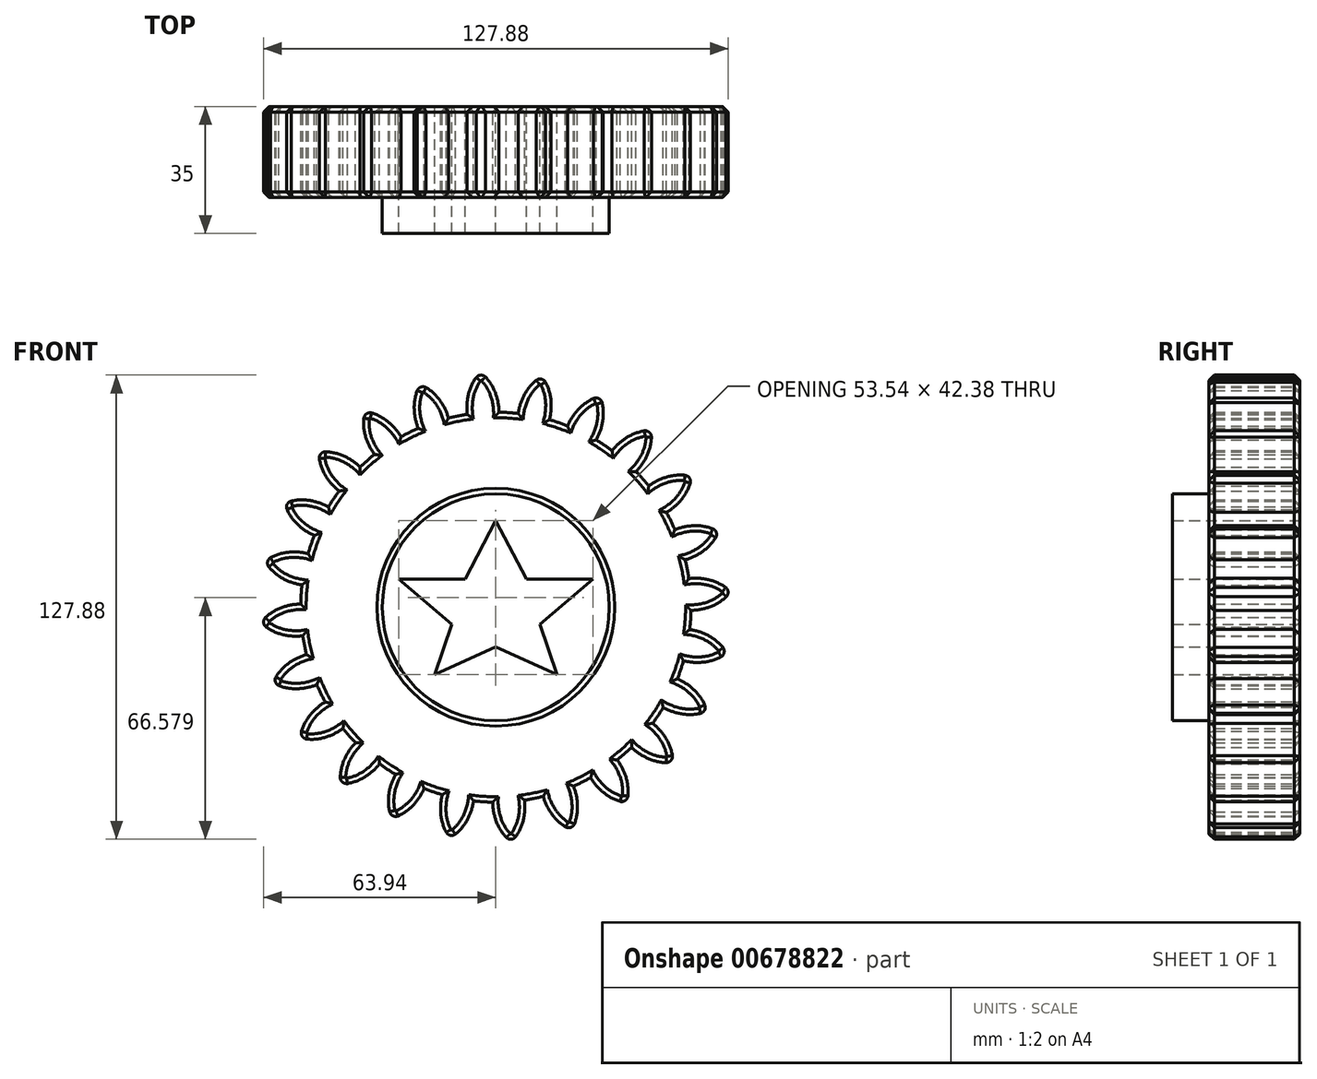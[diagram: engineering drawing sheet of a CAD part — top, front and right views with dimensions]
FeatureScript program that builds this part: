
annotation { "Feature Type Name" : "Feature", "Feature Type Description" : "" }
export const myFeature = defineFeature(function(context is Context, id is Id, definition is map)
    precondition{}
    {
        {
            var Q0;
            Q0=qCreatedBy(makeId("Front.planeOp"),FACE);
            var sketch = newSketch(context, id + "F0", { "sketchPlane" : qUnion([Q0])});
            skCircle(sketch, "E0", {"center": v(0, 0) * mm, "radius": 53.72 * mm});
            skCircle(sketch, "E1", {"center": v(0, 0) * mm, "radius": 58.67 * mm, "construction": true});
            skCircle(sketch, "E2", {"center": v(0, 0) * mm, "radius": 63.5 * mm, "construction": true});
            skLineSegment(sketch, "E3", {"start": v(0, 0) * mm, "end": v(0, 90.28) * mm, "construction": true});
            skLineSegment(sketch, "E4", {"start": v(0, 0) * mm, "end": v(-5.89, 89.83) * mm, "construction": true});
            skLineSegment(sketch, "E5", {"start": v(0, 58.67) * mm, "end": v(-86.47, 27.2) * mm, "construction": true});
            skLineSegment(sketch, "E6", {"start": v(0, 58.67) * mm, "end": v(-89.07, 58.67) * mm, "construction": true});
            skCircle(sketch, "E7", {"center": v(0, 0) * mm, "radius": 55.14 * mm, "construction": true});
            skCircle(sketch, "E8", {"center": v(0, 58.67) * mm, "radius": 14.6 * mm, "construction": true});
            skCircle(sketch, "E9", {"center": v(-13.72, 53.68) * mm, "radius": 14.6 * mm, "construction": true});
            skArc(sketch, "E10", {"start": v(0, 58.67) * mm, "mid": v(-1.18, 61.2) * mm, "end": v(-2.86, 63.44) * mm});
            skArc(sketch, "E11", {"start": v(0.88, 53.71) * mm, "mid": v(0.64, 56.23) * mm, "end": v(0, 58.67) * mm});
            skArc(sketch, "E12.MirrorCS", {"start": v(-7.88, 53.14) * mm, "mid": v(-7.97, 55.66) * mm, "end": v(-7.66, 58.17) * mm});
            skArc(sketch, "E13.MirrorCS", {"start": v(-7.66, 58.17) * mm, "mid": v(-6.82, 60.83) * mm, "end": v(-5.45, 63.27) * mm});
            skArc(sketch, "E14", {"start": v(-2.86, 63.44) * mm, "mid": v(-4.2, 63.93) * mm, "end": v(-5.45, 63.27) * mm});
            skCircle(sketch, "E15", {"center": v(0, 0) * mm, "radius": 31.25 * mm});
            skLineSegment(sketch, "E16", {"start": v(0, 23.83) * mm, "end": v(8.38, 7.72) * mm});
            skLineSegment(sketch, "E17", {"start": v(8.38, 7.72) * mm, "end": v(26.77, 7.72) * mm});
            skLineSegment(sketch, "E18", {"start": v(26.77, 7.72) * mm, "end": v(12.19, -4.72) * mm});
            skLineSegment(sketch, "E19", {"start": v(12.19, -4.72) * mm, "end": v(16.83, -18.55) * mm});
            skLineSegment(sketch, "E20", {"start": v(16.83, -18.55) * mm, "end": v(0, -10.88) * mm});
            skLineSegment(sketch, "E21.MirrorCS", {"start": v(0, 23.83) * mm, "end": v(-8.38, 7.72) * mm});
            skLineSegment(sketch, "E22.MirrorCS", {"start": v(-8.38, 7.72) * mm, "end": v(-26.77, 7.72) * mm});
            skLineSegment(sketch, "E23.MirrorCS", {"start": v(-26.77, 7.72) * mm, "end": v(-12.19, -4.72) * mm});
            skLineSegment(sketch, "E24.MirrorCS", {"start": v(-12.19, -4.72) * mm, "end": v(-16.83, -18.55) * mm});
            skLineSegment(sketch, "E25.MirrorCS", {"start": v(-16.83, -18.55) * mm, "end": v(0, -10.88) * mm});
            skSolve(sketch);
        }
        {
            var Q0;
            {var subQ0=sQuery(id+"F0.wireOp",EDGE,"E0");var subQ1=makeQuery(id+"F0.imprint","INTERSECT",VERTEX,{"derivedFrom":[subQ0,sQuery(id+"F0.wireOp",EDGE,"E12.MirrorCS")]});Q0=makeQuery(id+"F0.imprint","IMPRINT",FACE,{"disambiguationData":[TD([[makeQuery(id+"F0.imprint","IMPRINT",EDGE,{"disambiguationData":[TD([[subQ1,1.0]])],"derivedFrom":subQ0}),1.0]])]});}
            var Q1;
            Q1=makeQuery(id+"F0.imprint","IMPRINT",FACE,{"disambiguationData":[TD([[makeQuery(id+"F0.imprint","IMPRINT",EDGE,{"derivedFrom":sQuery(id+"F0.wireOp",EDGE,"E10")}),1.0]])]});
            extrude(context, id + "F1", {"entities" : qUnion([Q0, Q1]), "depth" : 25 * mm, "offsetDistance" : 25 * mm});
        }
        {
            var Q0;
            Q0=makeQuery(id+"F1.opExtrude","SWEPT_BODY",BODY,{"disambiguationData":[OSD([sQuery(id+"F0.wireOp",EDGE,"E0"),sQuery(id+"F0.wireOp",EDGE,"E10"),sQuery(id+"F0.wireOp",EDGE,"E12.MirrorCS"),sQuery(id+"F0.wireOp",EDGE,"E13.MirrorCS"),sQuery(id+"F0.wireOp",EDGE,"E11"),sQuery(id+"F0.wireOp",EDGE,"E14")])]});
            var Q1;
            Q1=makeQuery(id+"F1.opExtrude","SWEPT_FACE",FACE,{"disambiguationData":[OSD([sQuery(id+"F0.wireOp",EDGE,"E0")])]});
            circularPattern(context, id + "F2", {"entities" : qUnion([Q0]), "axis" : qUnion([Q1]), "angle" : 360 * degree, "instanceCount" : 24, "equalSpace" : true});
        }
        {
            var Q0;
            {var subQ0=makeQuery(id+"F1.opExtrude","CAP_FACE",FACE,{"disambiguationData":[OSD([sQuery(id+"F0.wireOp",EDGE,"E0"),sQuery(id+"F0.wireOp",EDGE,"E10"),sQuery(id+"F0.wireOp",EDGE,"E12.MirrorCS"),sQuery(id+"F0.wireOp",EDGE,"E13.MirrorCS"),sQuery(id+"F0.wireOp",EDGE,"E11"),sQuery(id+"F0.wireOp",EDGE,"E14"),sQuery(id+"F0.wireOp",EDGE,"E16"),sQuery(id+"F0.wireOp",EDGE,"E17"),sQuery(id+"F0.wireOp",EDGE,"E18"),sQuery(id+"F0.wireOp",EDGE,"E19"),sQuery(id+"F0.wireOp",EDGE,"E20"),sQuery(id+"F0.wireOp",EDGE,"E21.MirrorCS"),sQuery(id+"F0.wireOp",EDGE,"E22.MirrorCS"),sQuery(id+"F0.wireOp",EDGE,"E23.MirrorCS"),sQuery(id+"F0.wireOp",EDGE,"E24.MirrorCS"),sQuery(id+"F0.wireOp",EDGE,"E25.MirrorCS")])],"isStart":false});Q0=makeQuery(id+"FgwtWg0tSMJMYA0_0.boolean.opBoolean","MERGE",FACE,{"derivedFrom":[subQ0,makeQuery(id+"F2.opPattern","COPY",FACE,{"derivedFrom":subQ0,"instanceName":"1"}),makeQuery(id+"F2.opPattern","COPY",FACE,{"derivedFrom":subQ0,"instanceName":"2"}),makeQuery(id+"F2.opPattern","COPY",FACE,{"derivedFrom":subQ0,"instanceName":"3"}),makeQuery(id+"F2.opPattern","COPY",FACE,{"derivedFrom":subQ0,"instanceName":"4"}),makeQuery(id+"F2.opPattern","COPY",FACE,{"derivedFrom":subQ0,"instanceName":"5"}),makeQuery(id+"F2.opPattern","COPY",FACE,{"derivedFrom":subQ0,"instanceName":"6"}),makeQuery(id+"F2.opPattern","COPY",FACE,{"derivedFrom":subQ0,"instanceName":"7"}),makeQuery(id+"F2.opPattern","COPY",FACE,{"derivedFrom":subQ0,"instanceName":"8"}),makeQuery(id+"F2.opPattern","COPY",FACE,{"derivedFrom":subQ0,"instanceName":"9"}),makeQuery(id+"F2.opPattern","COPY",FACE,{"derivedFrom":subQ0,"instanceName":"10"}),makeQuery(id+"F2.opPattern","COPY",FACE,{"derivedFrom":subQ0,"instanceName":"11"}),makeQuery(id+"F2.opPattern","COPY",FACE,{"derivedFrom":subQ0,"instanceName":"12"}),makeQuery(id+"F2.opPattern","COPY",FACE,{"derivedFrom":subQ0,"instanceName":"13"}),makeQuery(id+"F2.opPattern","COPY",FACE,{"derivedFrom":subQ0,"instanceName":"14"}),makeQuery(id+"F2.opPattern","COPY",FACE,{"derivedFrom":subQ0,"instanceName":"15"}),makeQuery(id+"F2.opPattern","COPY",FACE,{"derivedFrom":subQ0,"instanceName":"16"}),makeQuery(id+"F2.opPattern","COPY",FACE,{"derivedFrom":subQ0,"instanceName":"17"}),makeQuery(id+"F2.opPattern","COPY",FACE,{"derivedFrom":subQ0,"instanceName":"18"}),makeQuery(id+"F2.opPattern","COPY",FACE,{"derivedFrom":subQ0,"instanceName":"19"}),makeQuery(id+"F2.opPattern","COPY",FACE,{"derivedFrom":subQ0,"instanceName":"20"}),makeQuery(id+"F2.opPattern","COPY",FACE,{"derivedFrom":subQ0,"instanceName":"21"}),makeQuery(id+"F2.opPattern","COPY",FACE,{"derivedFrom":subQ0,"instanceName":"22"}),makeQuery(id+"F2.opPattern","COPY",FACE,{"derivedFrom":subQ0,"instanceName":"23"})]});}
            var Q1;
            {var subQ0=sQuery(id+"F0.wireOp",EDGE,"E25.MirrorCS");var subQ1=sQuery(id+"F0.wireOp",EDGE,"E24.MirrorCS");var subQ2=sQuery(id+"F0.wireOp",EDGE,"E23.MirrorCS");var subQ3=sQuery(id+"F0.wireOp",EDGE,"E22.MirrorCS");var subQ4=sQuery(id+"F0.wireOp",EDGE,"E21.MirrorCS");var subQ5=sQuery(id+"F0.wireOp",EDGE,"E20");var subQ6=sQuery(id+"F0.wireOp",EDGE,"E19");var subQ7=sQuery(id+"F0.wireOp",EDGE,"E18");var subQ8=sQuery(id+"F0.wireOp",EDGE,"E17");var subQ9=sQuery(id+"F0.wireOp",EDGE,"E16");var subQ10=makeQuery(id+"F1.opExtrude","CAP_FACE",FACE,{"disambiguationData":[OSD([sQuery(id+"F0.wireOp",EDGE,"E0"),sQuery(id+"F0.wireOp",EDGE,"E10"),sQuery(id+"F0.wireOp",EDGE,"E12.MirrorCS"),sQuery(id+"F0.wireOp",EDGE,"E13.MirrorCS"),sQuery(id+"F0.wireOp",EDGE,"E11"),sQuery(id+"F0.wireOp",EDGE,"E14"),subQ9,subQ8,subQ7,subQ6,subQ5,subQ4,subQ3,subQ2,subQ1,subQ0])],"isStart":true});Q1=makeQuery(id+"FgwtWg0tSMJMYA0_0.boolean.opBoolean","MERGE",FACE,{"derivedFrom":[subQ10,makeQuery(id+"F2.opPattern","COPY",FACE,{"derivedFrom":subQ10,"instanceName":"1"}),makeQuery(id+"F2.opPattern","COPY",FACE,{"derivedFrom":subQ10,"instanceName":"2"}),makeQuery(id+"F2.opPattern","COPY",FACE,{"derivedFrom":subQ10,"instanceName":"3"}),makeQuery(id+"F2.opPattern","COPY",FACE,{"derivedFrom":subQ10,"instanceName":"4"}),makeQuery(id+"F2.opPattern","COPY",FACE,{"derivedFrom":subQ10,"instanceName":"5"}),makeQuery(id+"F2.opPattern","COPY",FACE,{"derivedFrom":subQ10,"instanceName":"6"}),makeQuery(id+"F2.opPattern","COPY",FACE,{"derivedFrom":subQ10,"instanceName":"7"}),makeQuery(id+"F2.opPattern","COPY",FACE,{"derivedFrom":subQ10,"instanceName":"8"}),makeQuery(id+"F2.opPattern","COPY",FACE,{"derivedFrom":subQ10,"instanceName":"9"}),makeQuery(id+"F2.opPattern","COPY",FACE,{"derivedFrom":subQ10,"instanceName":"10"}),makeQuery(id+"F2.opPattern","COPY",FACE,{"derivedFrom":subQ10,"instanceName":"11"}),makeQuery(id+"F2.opPattern","COPY",FACE,{"derivedFrom":subQ10,"instanceName":"12"}),makeQuery(id+"F2.opPattern","COPY",FACE,{"derivedFrom":subQ10,"instanceName":"13"}),makeQuery(id+"F2.opPattern","COPY",FACE,{"derivedFrom":subQ10,"instanceName":"14"}),makeQuery(id+"F2.opPattern","COPY",FACE,{"derivedFrom":subQ10,"instanceName":"15"}),makeQuery(id+"F2.opPattern","COPY",FACE,{"derivedFrom":subQ10,"instanceName":"16"}),makeQuery(id+"F2.opPattern","COPY",FACE,{"derivedFrom":subQ10,"instanceName":"17"}),makeQuery(id+"F2.opPattern","COPY",FACE,{"derivedFrom":subQ10,"instanceName":"18"}),makeQuery(id+"F2.opPattern","COPY",FACE,{"derivedFrom":subQ10,"instanceName":"19"}),makeQuery(id+"F2.opPattern","COPY",FACE,{"derivedFrom":subQ10,"instanceName":"20"}),makeQuery(id+"F2.opPattern","COPY",FACE,{"derivedFrom":subQ10,"instanceName":"21"}),makeQuery(id+"F2.opPattern","COPY",FACE,{"derivedFrom":subQ10,"instanceName":"22"}),makeQuery(id+"F2.opPattern","COPY",FACE,{"derivedFrom":subQ10,"instanceName":"23"}),makeQuery(id+"FgwtWg0tSMJMYA0_0.opExtrude","CAP_FACE",FACE,{"disambiguationData":[OSD([sQuery(id+"F0.wireOp",EDGE,"E15"),subQ9,subQ8,subQ7,subQ6,subQ5,subQ4,subQ3,subQ2,subQ1,subQ0])],"isStart":true})]});}
            chamfer(context, id + "F3", {"entities" : qUnion([Q0, Q1]), "width" : 1.5 * mm, "tangentPropagation" : true});
        }
        {
            var Q0;
            Q0=makeQuery(id+"F0.imprint","IMPRINT",FACE,{"disambiguationData":[TD([[makeQuery(id+"F0.imprint","IMPRINT",EDGE,{"derivedFrom":sQuery(id+"F0.wireOp",EDGE,"E15")}),1.0]])]});
            extrude(context, id + "F4", {"entities" : qUnion([Q0]), "operationType" : NewBodyOperationType.ADD, "depth" : 35 * mm, "offsetDistance" : 25 * mm});
        }
    });
